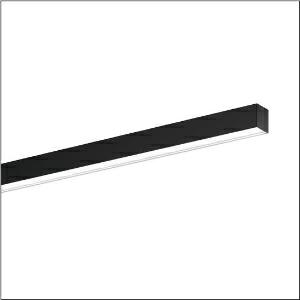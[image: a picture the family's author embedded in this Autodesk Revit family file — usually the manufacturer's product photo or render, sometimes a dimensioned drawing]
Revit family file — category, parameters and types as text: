
# Revit family: silica_21_51mx23dc4abb
name_source: partatom
category: Lighting Fixtures
units: mm (PartAtom-declared; Revit-internal decimal feet)

## family parameters
Cut with Voids When Loaded = No
Host = Face
Light Source = No
Part Type = Normal
Room Calculation Point = No
Round Connector Dimension = Use Diameter
Shared = No

## types (1)
- --- (1 x LED, 8200 lm, 58.2 W, 4000K)
    Apparent Load = 58 VA
    CIE Flux Codes = 78 96 99 100 100
    Color Rendering = 80
    Color Temperature = 4000K
    Default Elevation = 1800 mm
    Description = Silica 21, office luminaire, primary optical cover: prismatic diffuser, of PMMA, CAT 2 (L<= 3000cd/m²), light emission: direct distribution, primary light characteristic: symmetric, installation type: surface-mounted, LED, rated luminous flux: 8.200lm, luminous efficacy: 141lm/W, light colour: 840, colour temperature: 4000K, control gear: DALI 2, with terminal, 3+2-pole, max. 2.5mm², mains connection: 220..240V, AC, 50/60Hz, rated input power: 58.2W, luminaire housing, of aluminium, matt jet black (RAL 9005), length: 3.004mm, width: 53mm, height: 53mm, protection rating (complete): IP20, insulation class (complete): insulation class I (protective earthing), certification: CE, permissible operating ambient temperature: 0..+35°C, standard: EN 50419, packaging unit: 1 piece
    Height = 53 mm
    Lamp = 1 x LED
    Lamp Light Flux = 8200 lm
    Lamp Power = 58.2 W
    Lamp count = 1
    Length = 3004 mm
    Luminous efficacy = 141 lm/W
    Manufacturer = Siteco
    ModVariant = No
    Model = 51MX23DC4ABB
    Mounting Place = Ceiling
    Mounting Type = Surface mounted
    Number of Poles = 1
    OnlyDefault = Yes
    Power Factor = 1
    Product Name = Silica 21
    Product group = office luminaire | ceiling mounted
    ProductGroupID = 301
    Protection Class = Protection class I
    Protection Degree = IP 20
    RLX_Detail_Level = 1
    RLX_Emergency_Light_Flux = 0 lm
    RLX_Emergency_Type = 0
    RLX_Emergency_Type_DB = No
    RlxData = <blob elided: 23669 chars, md5=5bcd3a72>
    Socket = socket
    Standby Power = 0 W
    System Light Flux = 8200 lm
    System Power = 58 W
    Type Comments = factory setting: luminous flux: 100 % | dim-lin: 254 | 323 mA
    Type Image = l_1335925.jpg
    URL = http://relux.com
    VarID = @adj_121061
    Voltage = 0 V
    Weight = 0.00 kg
    Width = 53 mm

## geometry (parser evidence)
native form markers: Blend x4, Sweep x9
no freeform markers — native parametric forms only
